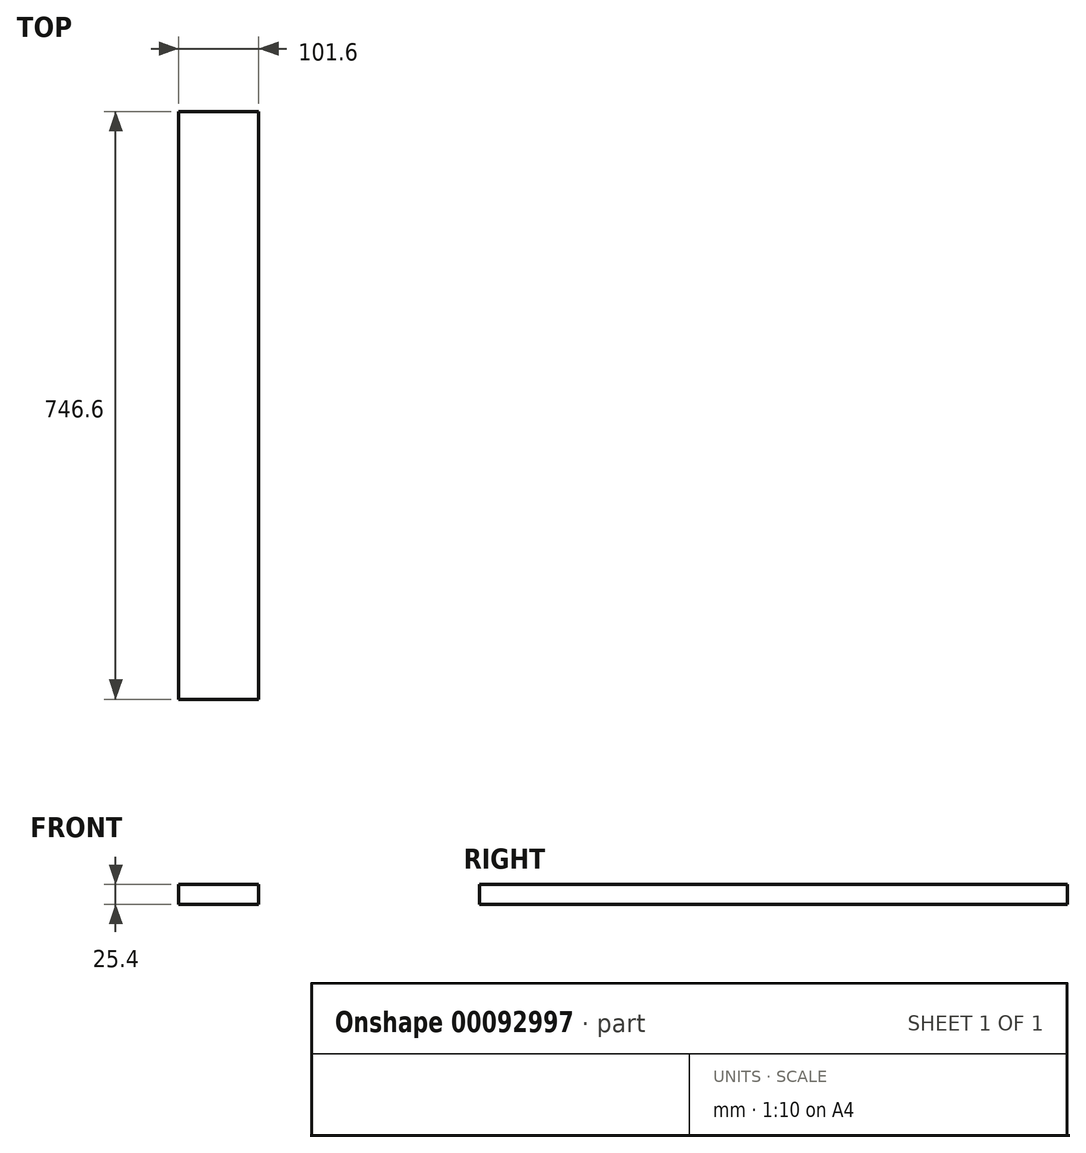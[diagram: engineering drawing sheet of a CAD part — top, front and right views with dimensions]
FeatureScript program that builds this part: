
annotation { "Feature Type Name" : "Feature", "Feature Type Description" : "" }
export const myFeature = defineFeature(function(context is Context, id is Id, definition is map)
    precondition{}
    {
        {
            var Q0;
            Q0=qCreatedBy(makeId("Front.planeOp"),FACE);
            var sketch = newSketch(context, id + "F0", { "sketchPlane" : qUnion([Q0])});
            skLineSegment(sketch, "E0.bottom", {"start": v(-50.8, 25.4) * mm, "end": v(50.8, 25.4) * mm});
            skLineSegment(sketch, "E0.top", {"start": v(-50.8, 0) * mm, "end": v(50.8, 0) * mm});
            skLineSegment(sketch, "E0.left", {"start": v(-50.8, 25.4) * mm, "end": v(-50.8, 0) * mm});
            skLineSegment(sketch, "E0.right", {"start": v(50.8, 25.4) * mm, "end": v(50.8, 0) * mm});
            skSolve(sketch);
        }
        {
            var Q0;
            Q0=qSketchRegion(id+"F0",true);
            var Q1;
            Q1=makeQuery(id+"F0.imprint","IMPRINT",FACE,{"disambiguationData":[TD([[makeQuery(id+"F0.imprint","IMPRINT",EDGE,{"derivedFrom":sQuery(id+"F0.wireOp",EDGE,"E0.bottom")}),-1.0]])]});
            extrude(context, id + "F1", {"entities" : qUnion([Q0, Q1]), "oppositeDirection" : true, "depth" : 746.6 * mm});
        }
    });
